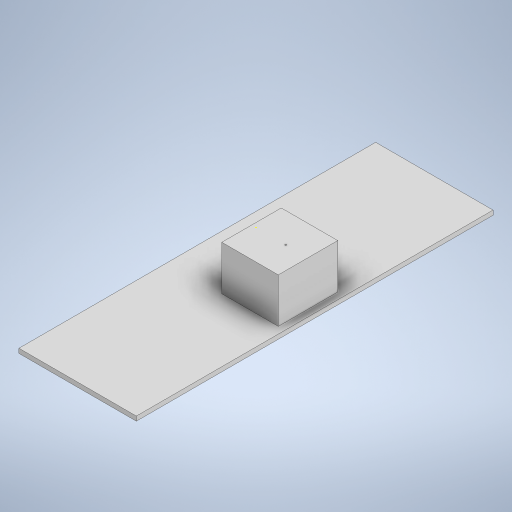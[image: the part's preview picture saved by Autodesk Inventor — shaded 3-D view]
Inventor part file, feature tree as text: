
AUTODESK INVENTOR PART (.ipt)
format: ipt  version: 2023 (Build 270158000, 158)  size: 259,584 bytes
history: native  units: mm
features: sketch x8, extrude x4
ambient origin geometry x8: Origin, YZ Plane, XZ Plane, XY Plane, X Axis, Y Axis, Z Axis, Center Point
bodies: Body1 (feature_tree)
feature tree (12):
  extrude  "Extrusion33"  Depth=240.0mm
  extrude  "Extrusion34"  Depth=38.0mm
  sketch  "Sketch46"  dims[d143=40.0mm d144=30.0mm d145=0.0mm]
  extrude  "Extrusion35"  Depth=30.0mm TaperAngle=0.0deg
  sketch  "Sketch48"  dims[d149=1.0mm]
  extrude  "Extrusion36"  Depth=30.0mm
  sketch  "Sketch55"  dims[d49=0.5mm]
  sketch  "Sketch56"  dims[d50=0.872665mm d51=0.5mm d52=0.872665mm d130=0.5mm d131=0.872665mm d132=0.5mm d133=0.872665mm d156=0.5mm d157=0.872665mm d158=0.5mm d159=0.872665mm]
  sketch  "Sketch44"  dims[d138=79.0mm d139=240.0mm]
  sketch  "Sketch45"  dims[d140=3.0mm d141=0.0mm d142=38.0mm]
  sketch  "Sketch47"  dims[d146=36.0mm d147=30.0mm d148=-2.617994mm]
  sketch  "Sketch49"  dims[d150=0.0mm d151=0.0mm]
